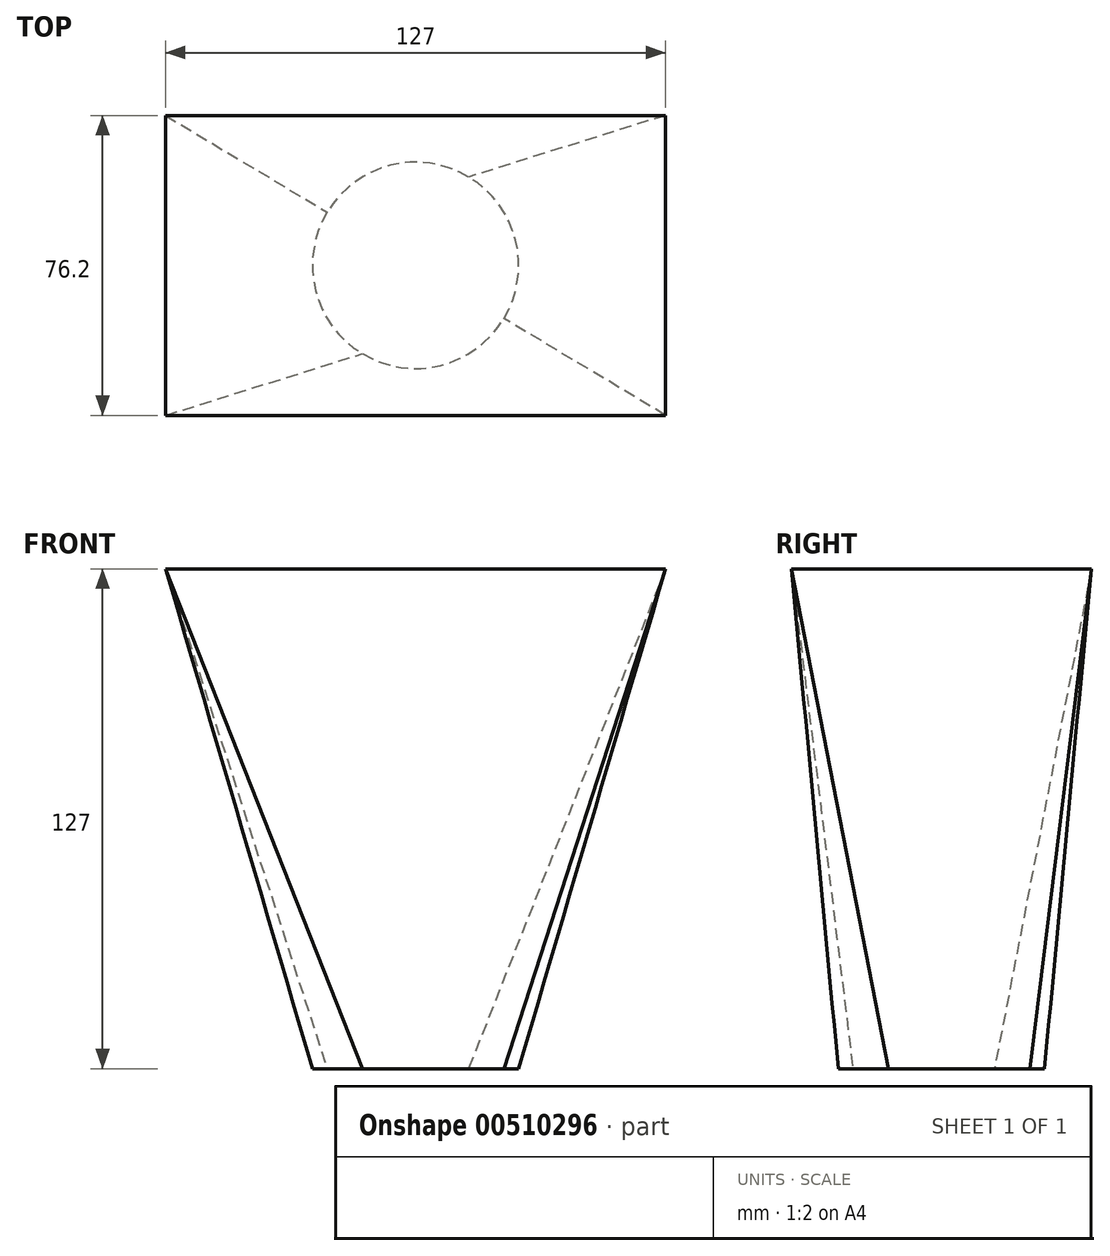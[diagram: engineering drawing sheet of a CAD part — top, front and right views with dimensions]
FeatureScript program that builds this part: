
annotation { "Feature Type Name" : "Feature", "Feature Type Description" : "" }
export const myFeature = defineFeature(function(context is Context, id is Id, definition is map)
    precondition{}
    {
        {
            var Q0;
            Q0=qCreatedBy(makeId("Top.planeOp"),FACE);
            var sketch = newSketch(context, id + "F0", { "sketchPlane" : qUnion([Q0])});
            skCircle(sketch, "E0", {"center": v(0, 0) * mm, "radius": 26.2 * mm});
            skSolve(sketch);
        }
        {
            var Q0;
            Q0=qCreatedBy(makeId("Top.planeOp"),FACE);
            cPlane(context, id + "F1", {"entities" : qUnion([Q0]), "cplaneType" : CPlaneType.OFFSET, "offset" : 127 * mm, "width" : 152.4 * mm, "height" : 152.4 * mm});
        }
        {
            var Q0;
            Q0=qCreatedBy(id+"F1.planeOp",FACE);
            var sketch = newSketch(context, id + "F2", { "sketchPlane" : qUnion([Q0])});
            skLineSegment(sketch, "E1.bottom", {"start": v(-63.5, 38.1) * mm, "end": v(63.5, 38.1) * mm});
            skLineSegment(sketch, "E1.top", {"start": v(-63.5, -38.1) * mm, "end": v(63.5, -38.1) * mm});
            skLineSegment(sketch, "E1.left", {"start": v(-63.5, 38.1) * mm, "end": v(-63.5, -38.1) * mm});
            skLineSegment(sketch, "E1.right", {"start": v(63.5, 38.1) * mm, "end": v(63.5, -38.1) * mm});
            skPoint(sketch, "E1.middle", {"position": v(0, 0) * mm});
            skSolve(sketch);
        }
        {
            var Q0;
            Q0=makeQuery(id+"F2.imprint","IMPRINT",FACE,{"disambiguationData":[TD([[makeQuery(id+"F2.imprint","IMPRINT",EDGE,{"derivedFrom":sQuery(id+"F2.wireOp",EDGE,"E1.bottom")}),-1.0]])]});
            var Q1;
            Q1=makeQuery(id+"F0.imprint","IMPRINT",FACE,{"disambiguationData":[TD([[makeQuery(id+"F0.imprint","IMPRINT",EDGE,{"derivedFrom":sQuery(id+"F0.wireOp",EDGE,"E0")}),1.0]])]});
            loft(context, id + "F3", {"sheetProfilesArray" : [{ "sheetProfileEntities" : qUnion([Q0]) }, { "sheetProfileEntities" : qUnion([Q1]) }]});
        }
    });
